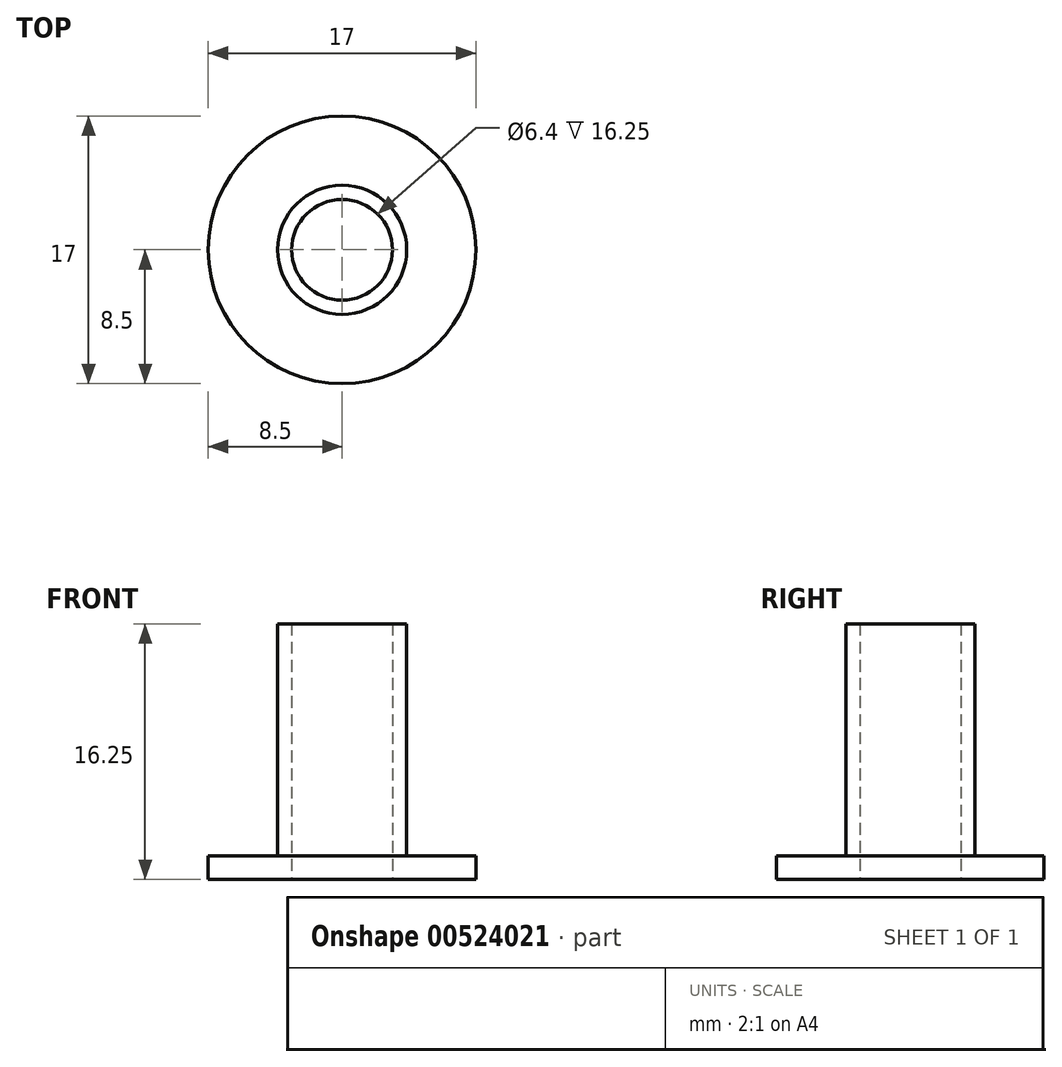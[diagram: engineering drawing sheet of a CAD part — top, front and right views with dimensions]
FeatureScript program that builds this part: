
annotation { "Feature Type Name" : "Feature", "Feature Type Description" : "" }
export const myFeature = defineFeature(function(context is Context, id is Id, definition is map)
    precondition{}
    {
        {
            var Q0;
            Q0=qCreatedBy(makeId("Top.planeOp"),FACE);
            var sketch = newSketch(context, id + "F0", { "sketchPlane" : qUnion([Q0])});
            skCircle(sketch, "E0", {"center": v(0, 0) * mm, "radius": 8.5 * mm});
            skCircle(sketch, "E1", {"center": v(0, 0) * mm, "radius": 4.1 * mm});
            skSolve(sketch);
        }
        {
            var Q0;
            Q0=makeQuery(id+"F0.imprint","IMPRINT",FACE,{"disambiguationData":[TD([[makeQuery(id+"F0.imprint","IMPRINT",EDGE,{"derivedFrom":sQuery(id+"F0.wireOp",EDGE,"E1")}),1.0]])]});
            extrude(context, id + "F1", {"entities" : qUnion([Q0]), "depth" : 16.25 * mm, "offsetDistance" : 25 * mm});
        }
        {
            var Q0;
            Q0 = qSketchRegion(id + "F0", true);
            extrude(context, id + "F2", {"entities" : qUnion([Q0]), "operationType" : NewBodyOperationType.ADD, "depth" : 1.5 * mm, "offsetDistance" : 25 * mm});
        }
        {
            var Q0;
            {var subQ0=sQuery(id+"F0.wireOp",EDGE,"E1");Q0=makeQuery(id+"F2.boolean.opBoolean","MERGE",FACE,{"derivedFrom":[makeQuery(id+"F1.opExtrude","CAP_FACE",FACE,{"disambiguationData":[OSD([subQ0])],"isStart":true}),makeQuery(id+"F2.opExtrude","CAP_FACE",FACE,{"disambiguationData":[OSD([sQuery(id+"F0.wireOp",EDGE,"E0"),subQ0])],"isStart":true})]});}
            var sketch = newSketch(context, id + "F3", { "sketchPlane" : qUnion([Q0])});
            skLineSegment(sketch, "E2", {"start": v(0, 0) * mm, "end": v(0, -5.76) * mm});
            skSolve(sketch);
        }
        {
            var Q0;
            Q0=sQuery(id+"F3.wireOp",VERTEX,"E2.start");
            var Q1;
            Q1=makeQuery(id+"F1.opExtrude","SWEPT_BODY",BODY,{"disambiguationData":[OSD([sQuery(id+"F0.wireOp",EDGE,"E1")])]});
            hole(context, id + "F4", {"style" : HoleStyle.SIMPLE, "endStyle" : HoleEndStyle.THROUGH, "holeDiameter" : 6.4 * mm, "isTappedThrough" : true, "tappedDepth" : 12 * mm, "tapClearance" : 3, "locations" : qUnion([Q0]), "scope" : qUnion([Q1])});
        }
    });
